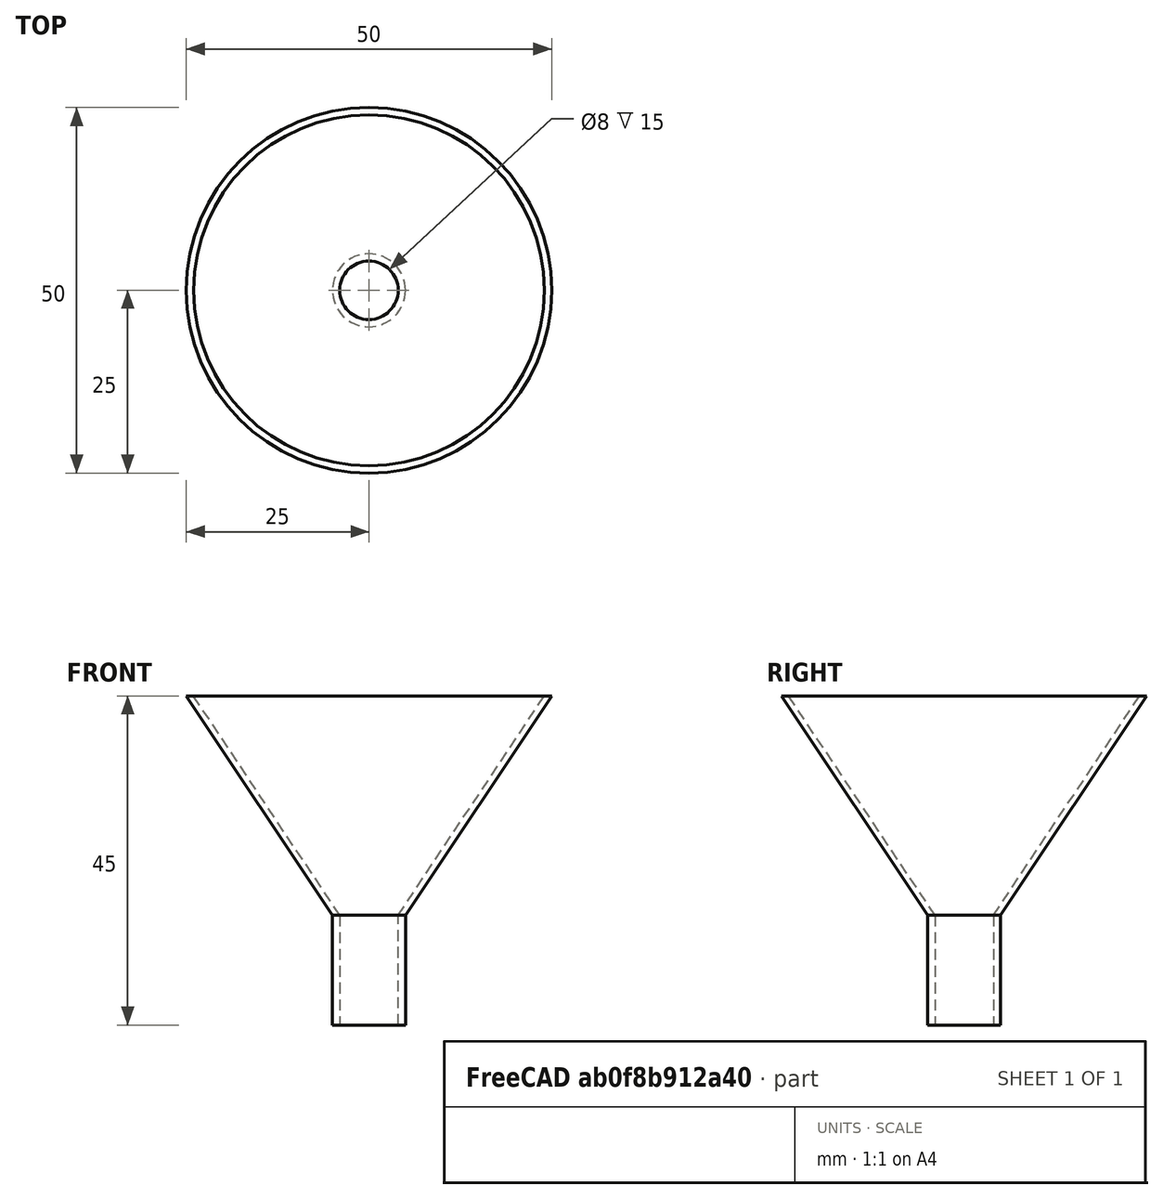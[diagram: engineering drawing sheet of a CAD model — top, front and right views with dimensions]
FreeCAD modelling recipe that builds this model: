
FCSTD DOCUMENT  (FreeCAD 1.0R39319 (Git))
Label: ojt1_t14r03_funnel
License: All rights reserved
LicenseURL: https://en.wikipedia.org/wiki/All_rights_reserved
objects: Part::Cylinder×2, Part::Cut×2, Part::Cone×2, Part::MultiFuse×1
note: 7 computed .brp shape members not serialized (recipe doc carries the construction recipe); baked Part::Feature solids carry a one-line shape summary decoded from their .brp

FEATURE [Part::Cylinder] Cylinder  label="Cilindre"
  Angle = 360
  AttacherType = Attacher::AttachEngine3D
  FirstAngle = 0
  Height = 15
  Radius = 5
  SecondAngle = 0
FEATURE [Part::Cylinder] Cylinder001  label="Cilindre001"
  Angle = 360
  AttacherType = Attacher::AttachEngine3D
  FirstAngle = 0
  Height = 15
  Radius = 4
  SecondAngle = 0
FEATURE [Part::Cut] Cut
  Base = -> Cylinder
  Refine = true
  Tool = -> Cylinder001
FEATURE [Part::Cone] Cone  label="Con"
  Angle = 360
  AttacherType = Attacher::AttachEngine3D
  Height = 30
  Placement = pos=(0,0,15) rot=(0,0,1;0rad)
  Radius1 = 5
  Radius2 = 25
FEATURE [Part::Cone] Cone001  label="Con001"
  Angle = 360
  AttacherType = Attacher::AttachEngine3D
  Height = 30
  Placement = pos=(0,0,15) rot=(0,0,1;0rad)
  Radius1 = 4
  Radius2 = 24
FEATURE [Part::Cut] Cut001
  Base = -> Cone
  Refine = true
  Tool = -> Cone001
FEATURE [Part::MultiFuse] Fusion
  Refine = true
  Shapes = -> [Cut,Cut001]
